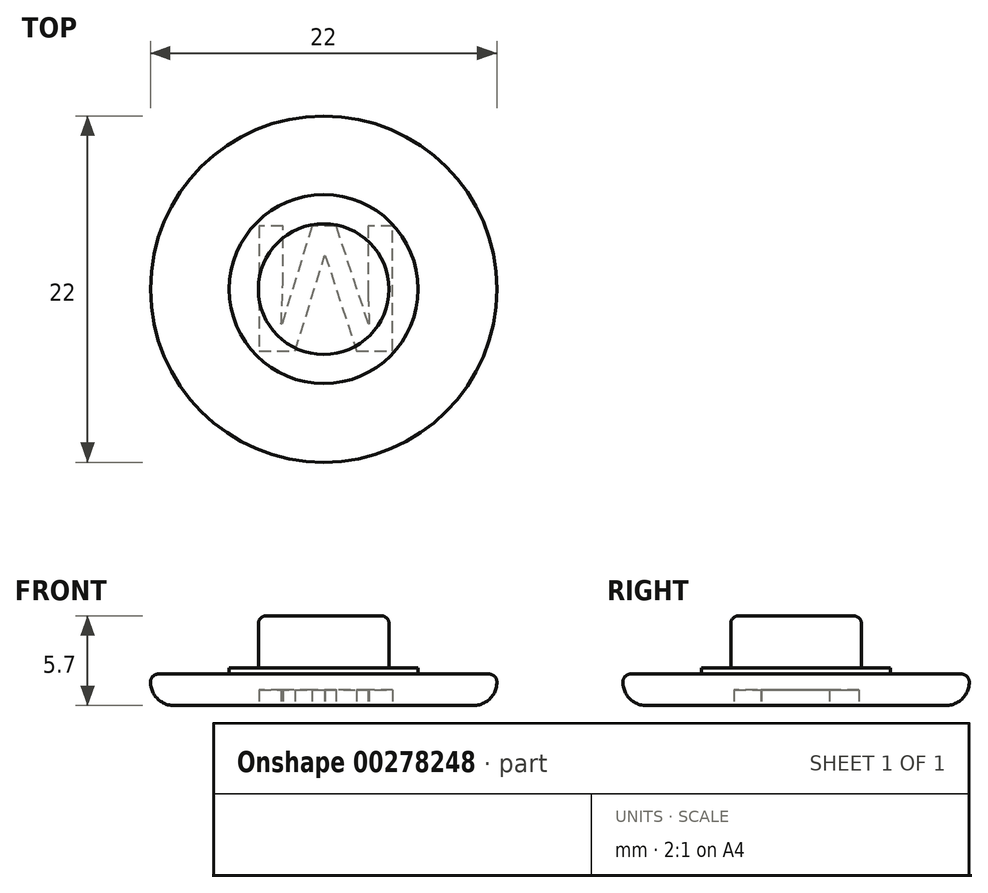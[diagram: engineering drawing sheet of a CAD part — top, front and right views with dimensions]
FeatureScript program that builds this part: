
annotation { "Feature Type Name" : "Feature", "Feature Type Description" : "" }
export const myFeature = defineFeature(function(context is Context, id is Id, definition is map)
    precondition{}
    {
        {
            var Q0;
            Q0=qCreatedBy(makeId("Top.planeOp"),FACE);
            var sketch = newSketch(context, id + "F0", { "sketchPlane" : qUnion([Q0])});
            skCircle(sketch, "E0", {"center": v(0, 0) * mm, "radius": 4.15 * mm});
            skCircle(sketch, "E1", {"center": v(0, 0) * mm, "radius": 11 * mm});
            skCircle(sketch, "E2", {"center": v(0, 0) * mm, "radius": 6 * mm});
            skSolve(sketch);
        }
        {
            var Q0;
            Q0=makeQuery(id+"F0.imprint","IMPRINT",FACE,{"disambiguationData":[TD([[makeQuery(id+"F0.imprint","IMPRINT",EDGE,{"derivedFrom":sQuery(id+"F0.wireOp",EDGE,"E1")}),1.0]])]});
            var Q1;
            Q1=makeQuery(id+"F0.imprint","IMPRINT",FACE,{"disambiguationData":[TD([[makeQuery(id+"F0.imprint","IMPRINT",EDGE,{"derivedFrom":sQuery(id+"F0.wireOp",EDGE,"E0")}),-1.0]])]});
            var Q2;
            Q2=makeQuery(id+"F0.imprint","IMPRINT",FACE,{"disambiguationData":[TD([[makeQuery(id+"F0.imprint","IMPRINT",EDGE,{"derivedFrom":sQuery(id+"F0.wireOp",EDGE,"E0")}),1.0]])]});
            extrude(context, id + "F1", {"entities" : qUnion([Q0, Q1, Q2]), "depth" : 2 * mm, "offsetDistance" : 25 * mm});
        }
        {
            var Q0;
            Q0=makeQuery(id+"F0.imprint","IMPRINT",FACE,{"disambiguationData":[TD([[makeQuery(id+"F0.imprint","IMPRINT",EDGE,{"derivedFrom":sQuery(id+"F0.wireOp",EDGE,"E0")}),-1.0]])]});
            extrude(context, id + "F2", {"entities" : qUnion([Q0]), "operationType" : NewBodyOperationType.ADD, "depth" : 2.4 * mm, "offsetDistance" : 25 * mm});
        }
        {
            var Q0;
            Q0=makeQuery(id+"F0.imprint","IMPRINT",FACE,{"disambiguationData":[TD([[makeQuery(id+"F0.imprint","IMPRINT",EDGE,{"derivedFrom":sQuery(id+"F0.wireOp",EDGE,"E0")}),1.0]])]});
            extrude(context, id + "F3", {"entities" : qUnion([Q0]), "operationType" : NewBodyOperationType.ADD, "depth" : 5.7 * mm, "offsetDistance" : 25 * mm});
        }
        {
            var Q0;
            Q0=makeQuery(id+"F1.opExtrude","CAP_EDGE",EDGE,{"disambiguationData":[OSD([sQuery(id+"F0.wireOp",EDGE,"E1")])],"isStart":false});
            fillet(context, id + "F4", {"entities" : qUnion([Q0]), "radius" : .5 * mm, "tangentPropagation" : true, "allowEdgeOverflow" : false});
        }
        {
            var Q0;
            Q0=makeQuery(id+"F3.opExtrude","CAP_EDGE",EDGE,{"disambiguationData":[OSD([sQuery(id+"F0.wireOp",EDGE,"E0")])],"isStart":false});
            fillet(context, id + "F5", {"entities" : qUnion([Q0]), "radius" : .5 * mm, "tangentPropagation" : true, "allowEdgeOverflow" : false});
        }
        {
            var Q0;
            Q0=makeQuery(id+"F1.opExtrude","CAP_EDGE",EDGE,{"disambiguationData":[OSD([sQuery(id+"F0.wireOp",EDGE,"E1")])],"isStart":true});
            fillet(context, id + "F6", {"entities" : qUnion([Q0]), "radius" : 1.5 * mm, "tangentPropagation" : true, "allowEdgeOverflow" : false});
        }
        {
            var Q0;
            Q0=makeQuery(id+"F1.opExtrude","CAP_FACE",FACE,{"disambiguationData":[OSD([sQuery(id+"F0.wireOp",EDGE,"E1")])],"isStart":true});
            var sketch = newSketch(context, id + "F7", { "sketchPlane" : qUnion([Q0])});
            skText(sketch, "E3", { "text": "M", "fontName": "OpenSans-Bold.ttf"});
            skPoint(sketch, "E4", {"position": v(0, 0) * mm});
            const initialGuessF7  = {"E3": [-0.0051, -0.004, 1, 0, 0.008]};
            skSetInitialGuess(sketch, initialGuessF7);
            skSolve(sketch);
        }
        {
            var Q0;
            Q0=makeQuery(id+"F7.imprint","IMPRINT",FACE,{"disambiguationData":[TD([[makeQuery(id+"F7.imprint","IMPRINT",EDGE,{"derivedFrom":sQuery(id+"F7.wireOp",EDGE,"E3.sketch_text.stroke-0")}),-1.0]])]});
            extrude(context, id + "F8", {"entities" : qUnion([Q0]), "operationType" : NewBodyOperationType.REMOVE, "oppositeDirection" : true, "depth" : 1 * mm, "offsetDistance" : 25 * mm});
        }
    });
